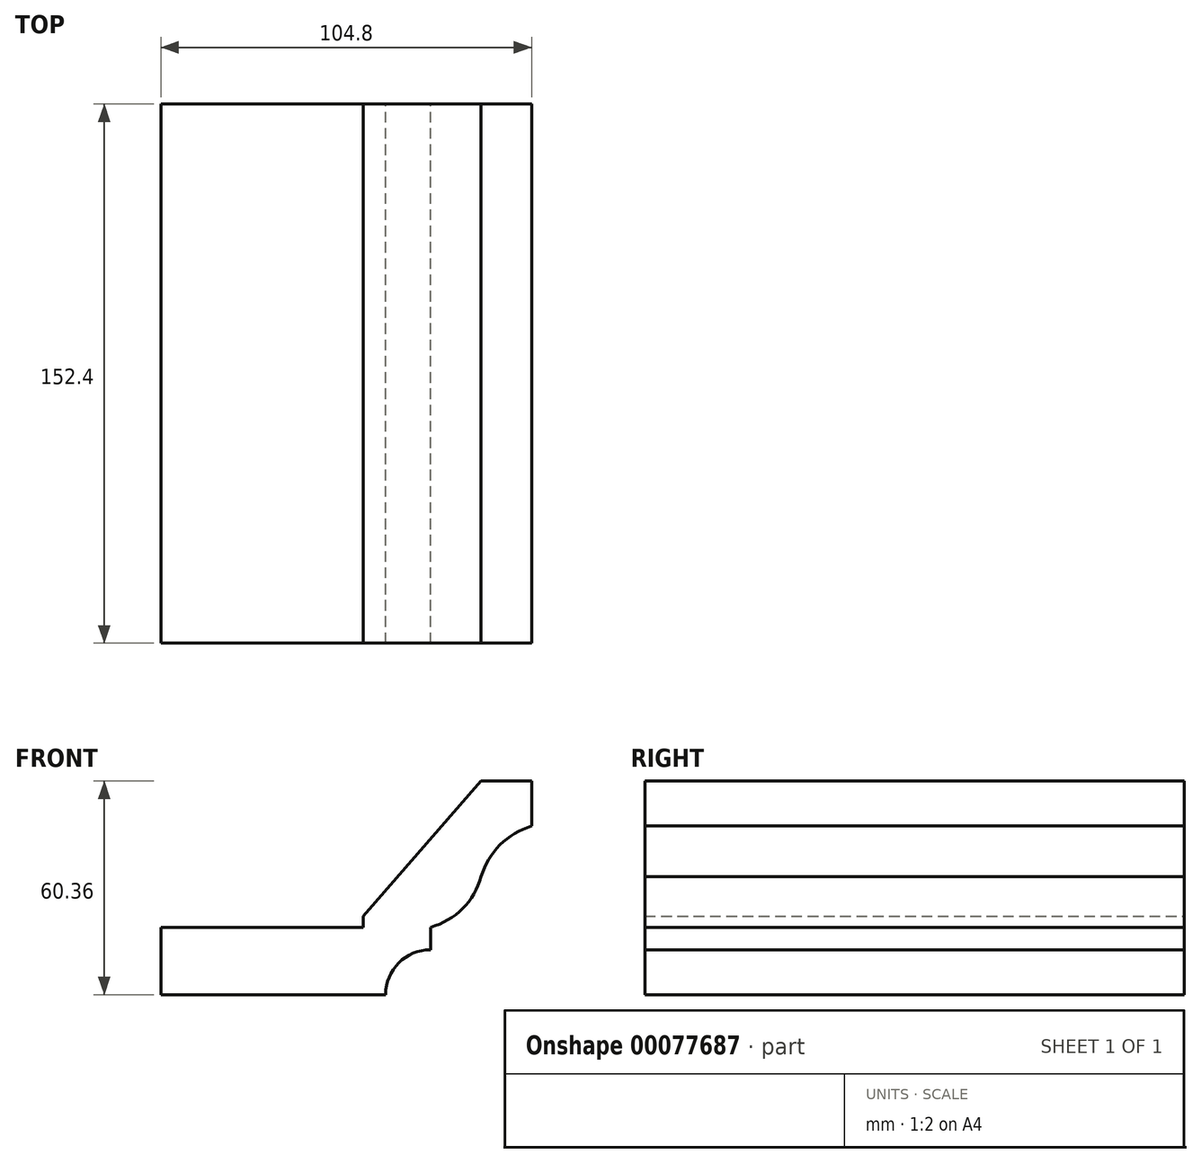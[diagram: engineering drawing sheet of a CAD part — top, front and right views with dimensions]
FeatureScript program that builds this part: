
annotation { "Feature Type Name" : "Feature", "Feature Type Description" : "" }
export const myFeature = defineFeature(function(context is Context, id is Id, definition is map)
    precondition{}
    {
        {
            var Q0;
            Q0=qCreatedBy(makeId("Front.planeOp"),FACE);
            var sketch = newSketch(context, id + "F0", { "sketchPlane" : qUnion([Q0])});
            skLineSegment(sketch, "E0", {"start": v(4.75, -30.18) * mm, "end": v(-52.4, -30.18) * mm});
            skLineSegment(sketch, "E1", {"start": v(-52.4, -30.18) * mm, "end": v(-52.4, -11.13) * mm});
            skLineSegment(sketch, "E2", {"start": v(-52.4, -11.13) * mm, "end": v(4.75, -11.13) * mm});
            skLineSegment(sketch, "E3", {"start": v(52.4, 30.18) * mm, "end": v(52.4, 17.47) * mm});
            skLineSegment(sketch, "E4", {"start": v(4.75, -30.18) * mm, "end": v(11.1, -30.18) * mm});
            skLineSegment(sketch, "E5", {"start": v(4.75, -30.18) * mm, "end": v(4.75, -7.94) * mm});
            skLineSegment(sketch, "E6", {"start": v(4.75, -7.94) * mm, "end": v(38.03, 30.18) * mm});
            skLineSegment(sketch, "E7", {"start": v(23.8, -17.47) * mm, "end": v(23.8, -11.12) * mm});
            skArc(sketch, "E8", {"start": v(23.8, -17.47) * mm, "mid": v(14.82, -21.2) * mm, "end": v(11.1, -30.18) * mm});
            skArc(sketch, "E9", {"start": v(23.8, -11.12) * mm, "mid": v(32.87, -5.88) * mm, "end": v(38.1, 3.18) * mm});
            skArc(sketch, "E10", {"start": v(52.4, 17.47) * mm, "mid": v(43.44, 12.14) * mm, "end": v(38.1, 3.18) * mm});
            skLineSegment(sketch, "E11", {"start": v(38.03, 30.18) * mm, "end": v(52.4, 30.18) * mm});
            skSolve(sketch);
        }
        {
            var Q0;
            Q0=makeQuery(id+"F0.imprint","IMPRINT",FACE,{"disambiguationData":[TD([[makeQuery(id+"F0.imprint","IMPRINT",EDGE,{"derivedFrom":sQuery(id+"F0.wireOp",EDGE,"E3")}),-1.0]])]});
            var Q1;
            {var subQ0=sQuery(id+"F0.wireOp",EDGE,"E0");Q1=makeQuery(id+"F0.imprint","IMPRINT",FACE,{"disambiguationData":[TD([[makeQuery(id+"F0.imprint","IMPRINT",EDGE,{"derivedFrom":subQ0}),-1.0]])]});}
            extrude(context, id + "F1", {"entities" : qUnion([Q0, Q1]), "depth" : 152.4 * mm});
        }
    });
